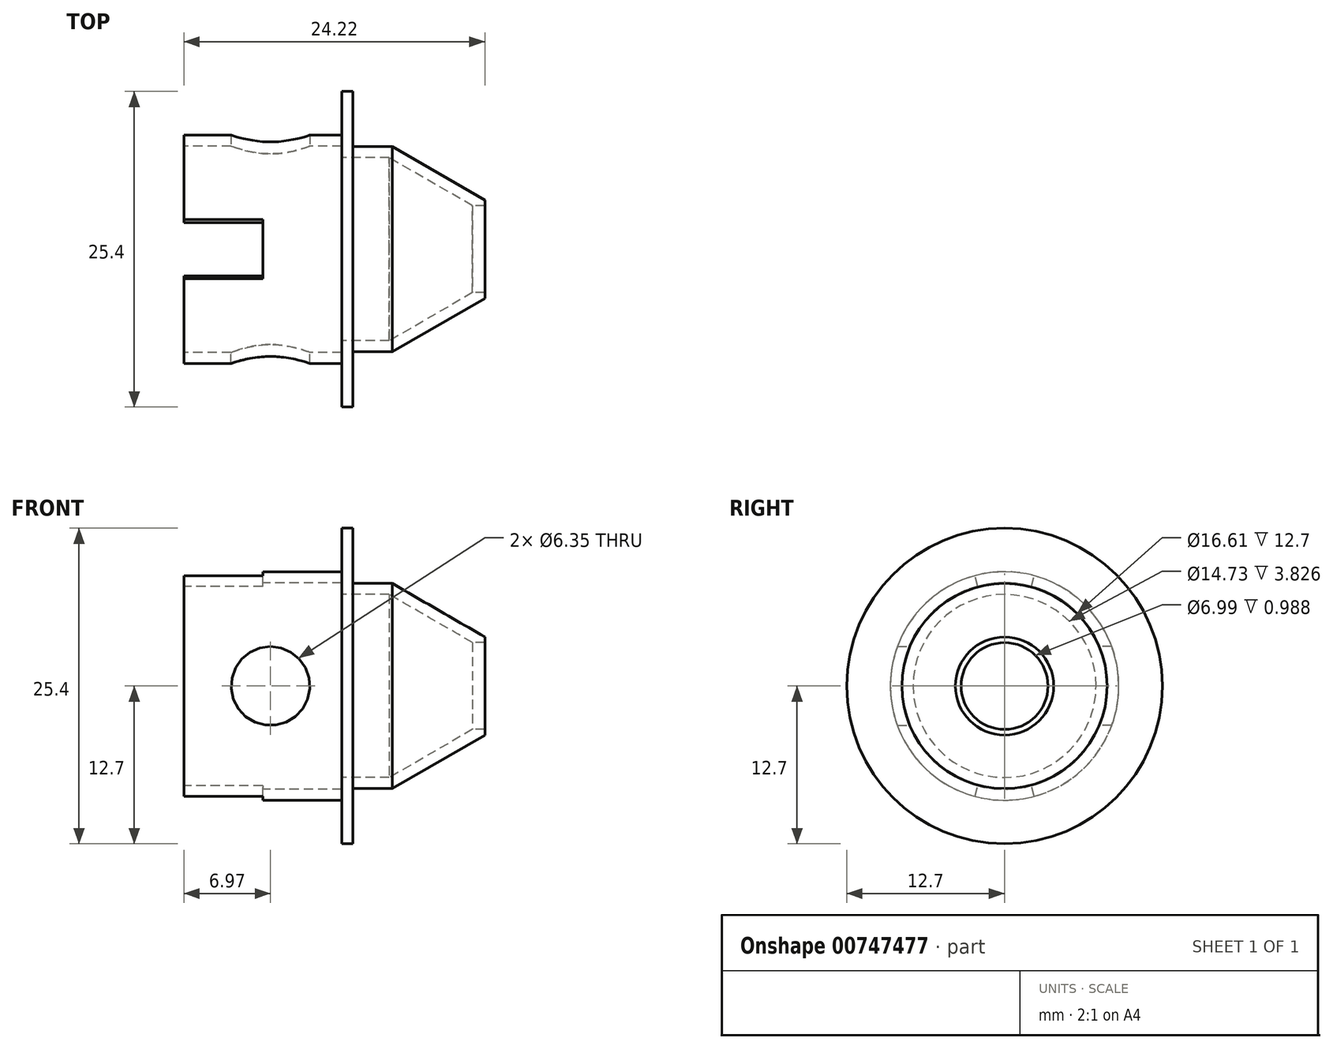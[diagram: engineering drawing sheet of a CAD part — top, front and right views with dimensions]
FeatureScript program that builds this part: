
annotation { "Feature Type Name" : "Feature", "Feature Type Description" : "" }
export const myFeature = defineFeature(function(context is Context, id is Id, definition is map)
    precondition{}
    {
        {
            var Q0;
            Q0=qCreatedBy(makeId("Front.planeOp"),FACE);
            var sketch = newSketch(context, id + "F0", { "sketchPlane" : qUnion([Q0])});
            skLineSegment(sketch, "E0", {"start": v(-20.11, 0) * mm, "end": v(19.6, 0) * mm, "construction": true});
            skLineSegment(sketch, "E1", {"start": v(-13.07, 12.7) * mm, "end": v(-12.19, 12.7) * mm});
            skLineSegment(sketch, "E2", {"start": v(-1.55, 3.95) * mm, "end": v(-9.01, 8.25) * mm});
            skPoint(sketch, "E3.orphan", {"position": v(-10.73, 12.7) * mm});
            skLineSegment(sketch, "E4", {"start": v(-9.01, 8.25) * mm, "end": v(-12.19, 8.25) * mm});
            skLineSegment(sketch, "E5", {"start": v(-12.19, 8.25) * mm, "end": v(-12.19, 12.7) * mm});
            skLineSegment(sketch, "E6.0", {"start": v(-2.54, 3.5) * mm, "end": v(-9.25, 7.37) * mm});
            skLineSegment(sketch, "E7.0", {"start": v(-9.25, 7.37) * mm, "end": v(-13.07, 7.37) * mm});
            skPoint(sketch, "E8.orphan", {"position": v(-12.19, 8.25) * mm});
            skPoint(sketch, "E9.orphan", {"position": v(-10.73, 3.5) * mm});
            skPoint(sketch, "E10.end.orphan", {"position": v(0, 3.05) * mm});
            skLineSegment(sketch, "E11.0", {"start": v(-13.07, 7.37) * mm, "end": v(-13.07, 8.3) * mm});
            skPoint(sketch, "E12.orphan", {"position": v(-15.95, 8.25) * mm});
            skLineSegment(sketch, "E13", {"start": v(-13.07, 8.3) * mm, "end": v(-25.77, 8.3) * mm});
            skLineSegment(sketch, "E14.0", {"start": v(-13.07, 9.2) * mm, "end": v(-25.77, 9.2) * mm});
            skLineSegment(sketch, "E15", {"start": v(-25.77, 8.3) * mm, "end": v(-25.77, 9.2) * mm});
            skPoint(sketch, "E16.orphan", {"position": v(-15.95, 12.7) * mm});
            skPoint(sketch, "E17.orphan", {"position": v(0, 12.7) * mm});
            skLineSegment(sketch, "E18.trimOffspring", {"start": v(-13.07, 9.2) * mm, "end": v(-13.07, 12.7) * mm});
            skLineSegment(sketch, "E19", {"start": v(-2.54, 3.5) * mm, "end": v(-1.55, 3.5) * mm});
            skLineSegment(sketch, "E20", {"start": v(-1.55, 3.5) * mm, "end": v(-1.55, 3.95) * mm});
            skSolve(sketch);
        }
        {
            var Q0;
            {var subQ0=sQuery(id+"F0.wireOp",EDGE,"E13");Q0=makeQuery(id+"F0.imprint","IMPRINT",FACE,{"disambiguationData":[TD([[makeQuery(id+"F0.imprint","IMPRINT",EDGE,{"derivedFrom":subQ0}),-1.0]])]});}
            var Q1;
            Q1=makeQuery(id+"F0.imprint","IMPRINT",FACE,{"disambiguationData":[TD([[makeQuery(id+"F0.imprint","IMPRINT",EDGE,{"derivedFrom":sQuery(id+"F0.wireOp",EDGE,"E2")}),1.0]])]});
            var Q2;
            {var subQ0=sQuery(id+"F0.wireOp",EDGE,"E5");var subQ1=sQuery(id+"F0.wireOp",EDGE,"E1");var subQ2=makeQuery(id+"F0.imprint","INTERSECT",VERTEX,{"derivedFrom":[subQ1,subQ0]});Q2=makeQuery(id+"F0.imprint","IMPRINT",FACE,{"disambiguationData":[TD([[makeQuery(id+"F0.imprint","IMPRINT",EDGE,{"disambiguationData":[TD([[subQ2,1.0]])],"derivedFrom":subQ1}),-1.0]])]});}
            var Q3;
            Q3=sQuery(id+"F0.wireOp",EDGE,"E0");
            revolve(context, id + "F1", {"surfaceOperationType" : NewSurfaceOperationType.NEW, "entities" : qUnion([Q0, Q1, Q2]), "axis" : qUnion([Q3]), "revolveType" : RevolveType.FULL});
        }
        {
            var Q0;
            Q0=makeQuery(id+"F1.opRevolve","SWEPT_FACE",FACE,{"disambiguationData":[OSD([sQuery(id+"F0.wireOp",EDGE,"E15")])]});
            var sketch = newSketch(context, id + "F2", { "sketchPlane" : qUnion([Q0])});
            skArc(sketch, "E21", {"start": v(2.38, 8.88) * mm, "mid": v(0, 9.2) * mm, "end": v(-2.38, 8.88) * mm});
            skArc(sketch, "E22", {"start": v(-2.15, -8.02) * mm, "mid": v(0, -8.3) * mm, "end": v(2.15, -8.02) * mm});
            skLineSegment(sketch, "E23", {"start": v(2.38, -8.88) * mm, "end": v(2.15, -8.02) * mm});
            skLineSegment(sketch, "E24.MirrorCS", {"start": v(-2.38, -8.88) * mm, "end": v(-2.15, -8.02) * mm});
            skLineSegment(sketch, "E25.trimOffspring", {"start": v(-2.15, 8.02) * mm, "end": v(-2.38, 8.88) * mm});
            skLineSegment(sketch, "E26.trimOffspring", {"start": v(2.15, 8.02) * mm, "end": v(2.38, 8.88) * mm});
            skArc(sketch, "E27.trimOffspring", {"start": v(2.15, 8.02) * mm, "mid": v(0, 8.3) * mm, "end": v(-2.15, 8.02) * mm});
            skArc(sketch, "E28.trimOffspring", {"start": v(-2.38, -8.88) * mm, "mid": v(0, -9.2) * mm, "end": v(2.38, -8.88) * mm});
            skSolve(sketch);
        }
        {
            var Q0;
            Q0=makeQuery(id+"F2.imprint","IMPRINT",FACE,{"disambiguationData":[TD([[makeQuery(id+"F2.imprint","IMPRINT",EDGE,{"derivedFrom":sQuery(id+"F2.wireOp",EDGE,"E21")}),1.0]])]});
            var Q1;
            Q1=makeQuery(id+"F2.imprint","IMPRINT",FACE,{"disambiguationData":[TD([[makeQuery(id+"F2.imprint","IMPRINT",EDGE,{"derivedFrom":sQuery(id+"F2.wireOp",EDGE,"E22")}),-1.0]])]});
            extrude(context, id + "F3", {"entities" : qUnion([Q0, Q1]), "operationType" : NewBodyOperationType.REMOVE, "oppositeDirection" : true, "depth" : 6.35 * mm, "offsetDistance" : 25.4 * mm});
        }
        {
            var Q0;
            Q0=qCreatedBy(makeId("Front.planeOp"),FACE);
            var sketch = newSketch(context, id + "F4", { "sketchPlane" : qUnion([Q0])});
            skCircle(sketch, "E29", {"center": v(-18.8, 0) * mm, "radius": 3.14 * mm});
            skSolve(sketch);
        }
        {
            var Q0;
            Q0=sQuery(id+"F4.wireOp",VERTEX,"E29.center");
            var Q1;
            Q1=makeQuery(id+"F1.opRevolve","SWEPT_BODY",BODY,{"disambiguationData":[OSD([sQuery(id+"F0.wireOp",EDGE,"E1"),sQuery(id+"F0.wireOp",EDGE,"E2"),sQuery(id+"F0.wireOp",EDGE,"E4"),sQuery(id+"F0.wireOp",EDGE,"E5"),sQuery(id+"F0.wireOp",EDGE,"E6.0"),sQuery(id+"F0.wireOp",EDGE,"E7.0"),sQuery(id+"F0.wireOp",EDGE,"E11.0"),sQuery(id+"F0.wireOp",EDGE,"E13"),sQuery(id+"F0.wireOp",EDGE,"E14.0"),sQuery(id+"F0.wireOp",EDGE,"E15"),sQuery(id+"F0.wireOp",EDGE,"E18.trimOffspring"),sQuery(id+"F0.wireOp",EDGE,"E19"),sQuery(id+"F0.wireOp",EDGE,"E20")])]});
            hole(context, id + "F5", {"style" : HoleStyle.SIMPLE, "endStyle" : HoleEndStyle.THROUGH, "holeDiameter" : 6.35 * mm, "majorDiameter" : 6.35 * mm, "isTappedThrough" : true, "tappedDepth" : 12.7 * mm, "tapClearance" : 3, "startFromSketch" : true, "locations" : qUnion([Q0]), "scope" : qUnion([Q1])});
        }
        {
            var Q0;
            Q0=sQuery(id+"F4.wireOp",VERTEX,"E29.center");
            var Q1;
            Q1=makeQuery(id+"F1.opRevolve","SWEPT_BODY",BODY,{"disambiguationData":[OSD([sQuery(id+"F0.wireOp",EDGE,"E1"),sQuery(id+"F0.wireOp",EDGE,"E2"),sQuery(id+"F0.wireOp",EDGE,"E4"),sQuery(id+"F0.wireOp",EDGE,"E5"),sQuery(id+"F0.wireOp",EDGE,"E6.0"),sQuery(id+"F0.wireOp",EDGE,"E7.0"),sQuery(id+"F0.wireOp",EDGE,"E11.0"),sQuery(id+"F0.wireOp",EDGE,"E13"),sQuery(id+"F0.wireOp",EDGE,"E14.0"),sQuery(id+"F0.wireOp",EDGE,"E15"),sQuery(id+"F0.wireOp",EDGE,"E18.trimOffspring"),sQuery(id+"F0.wireOp",EDGE,"E19"),sQuery(id+"F0.wireOp",EDGE,"E20")])]});
            hole(context, id + "F6", {"style" : HoleStyle.SIMPLE, "endStyle" : HoleEndStyle.THROUGH, "oppositeDirection" : true, "holeDiameter" : 6.35 * mm, "majorDiameter" : 6.35 * mm, "isTappedThrough" : true, "tappedDepth" : 12.7 * mm, "tapClearance" : 3, "startFromSketch" : true, "locations" : qUnion([Q0]), "scope" : qUnion([Q1])});
        }
    });
